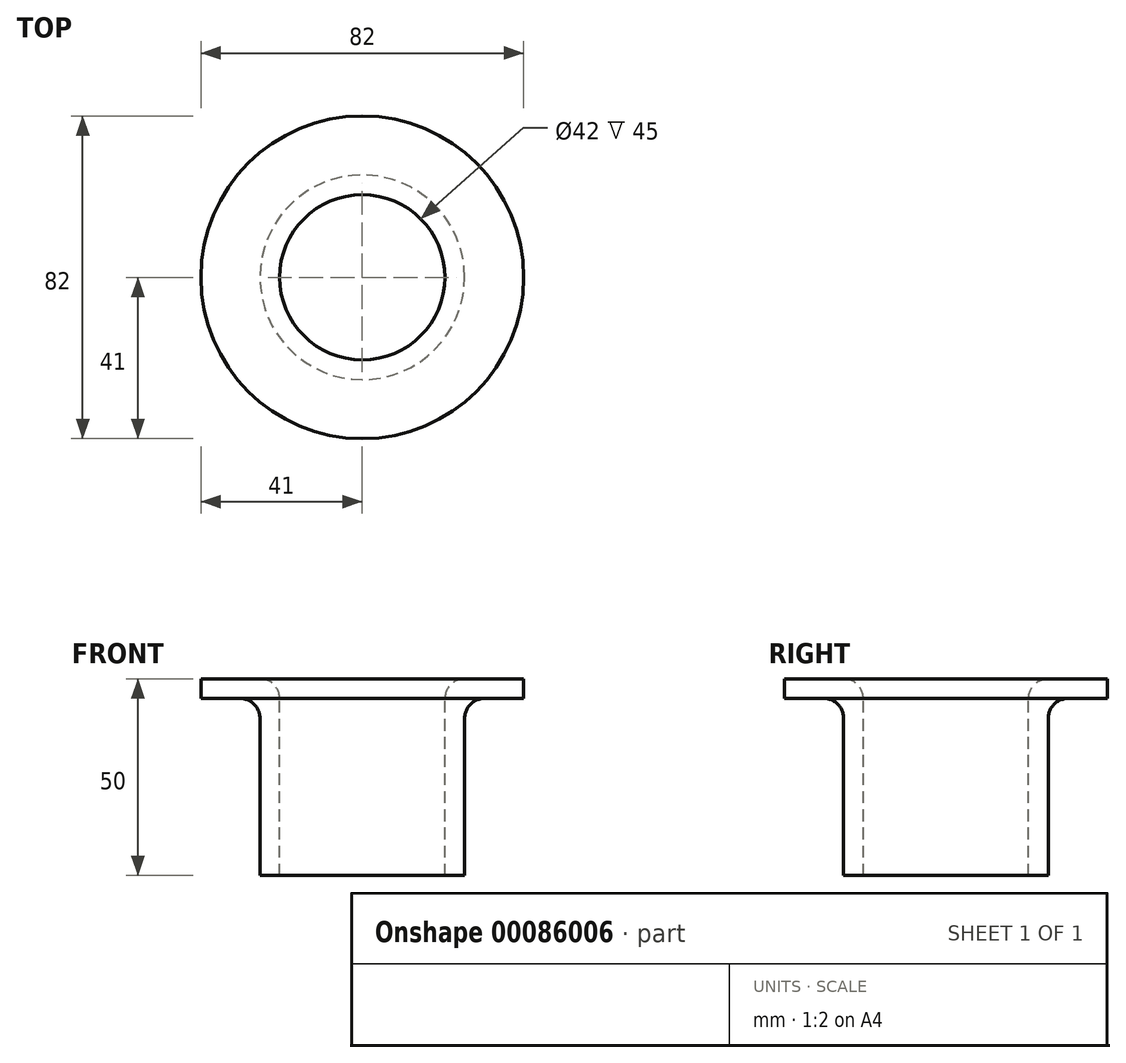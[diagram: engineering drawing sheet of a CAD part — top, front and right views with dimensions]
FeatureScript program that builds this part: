
annotation { "Feature Type Name" : "Feature", "Feature Type Description" : "" }
export const myFeature = defineFeature(function(context is Context, id is Id, definition is map)
    precondition{}
    {
        {
            var Q0;
            Q0=qCreatedBy(makeId("Front.planeOp"),FACE);
            var sketch = newSketch(context, id + "F0", { "sketchPlane" : qUnion([Q0])});
            skLineSegment(sketch, "E0", {"start": v(41, 0) * mm, "end": v(41, -5) * mm});
            skLineSegment(sketch, "E1", {"start": v(41, -5) * mm, "end": v(31, -5) * mm});
            skLineSegment(sketch, "E2", {"start": v(26, -10) * mm, "end": v(26, -50) * mm});
            skLineSegment(sketch, "E3", {"start": v(0, 0) * mm, "end": v(0, -50.07) * mm, "construction": true});
            skLineSegment(sketch, "E4", {"start": v(41, 0) * mm, "end": v(26, 0) * mm});
            skLineSegment(sketch, "E5", {"start": v(21, -5) * mm, "end": v(21, -50) * mm});
            skLineSegment(sketch, "E6", {"start": v(21, -50) * mm, "end": v(26, -50) * mm});
            skPoint(sketch, "E7.visualSharp", {"position": v(21, 0) * mm});
            skArc(sketch, "E7.filletArc", {"start": v(26, 0) * mm, "mid": v(22.46, -1.46) * mm, "end": v(21, -5) * mm});
            skArc(sketch, "E8.filletArc", {"start": v(31, -5) * mm, "mid": v(27.46, -6.46) * mm, "end": v(26, -10) * mm});
            skSolve(sketch);
        }
        {
            var Q0;
            Q0=makeQuery(id+"F0.imprint","IMPRINT",FACE,{"disambiguationData":[TD([[makeQuery(id+"F0.imprint","IMPRINT",EDGE,{"derivedFrom":sQuery(id+"F0.wireOp",EDGE,"E0")}),-1.0]])]});
            var Q1;
            Q1=sQuery(id+"F0.wireOp",EDGE,"E3");
            revolve(context, id + "F1", {"entities" : qUnion([Q0]), "axis" : qUnion([Q1]), "revolveType" : RevolveType.FULL});
        }
    });
